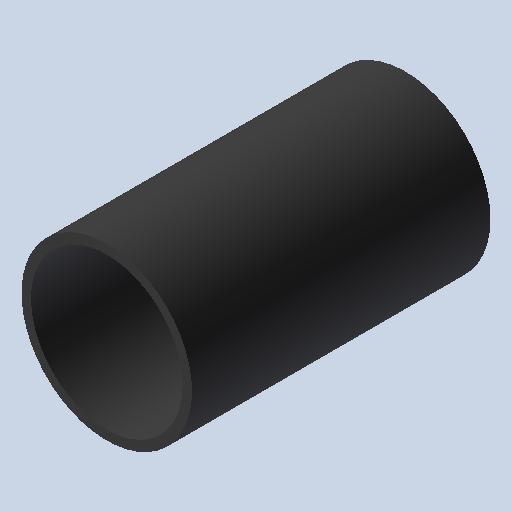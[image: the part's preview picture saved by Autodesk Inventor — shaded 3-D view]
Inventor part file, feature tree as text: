
AUTODESK INVENTOR PART (.ipt)
format: ipt  version: 2025.2 (Build 292293000, 293)  size: 125,952 bytes
history: native  units: in
note: dims shown in document units (in); Inventor stores cm internally (conversion verified against a paired STEP export)
features: extrude x1, sketch x1
ambient origin geometry x8: Origin, YZ Plane, XZ Plane, XY Plane, X Axis, Y Axis, Z Axis, Center Point
bodies: Solid1 (feature_tree)
feature tree (2):
  extrude  "Extrusion1"  Depth=1.9685in
  sketch  "Sketch1"  dims[d0=1.125in d1=1.0in d2=1.9685in d3=0.0in]
